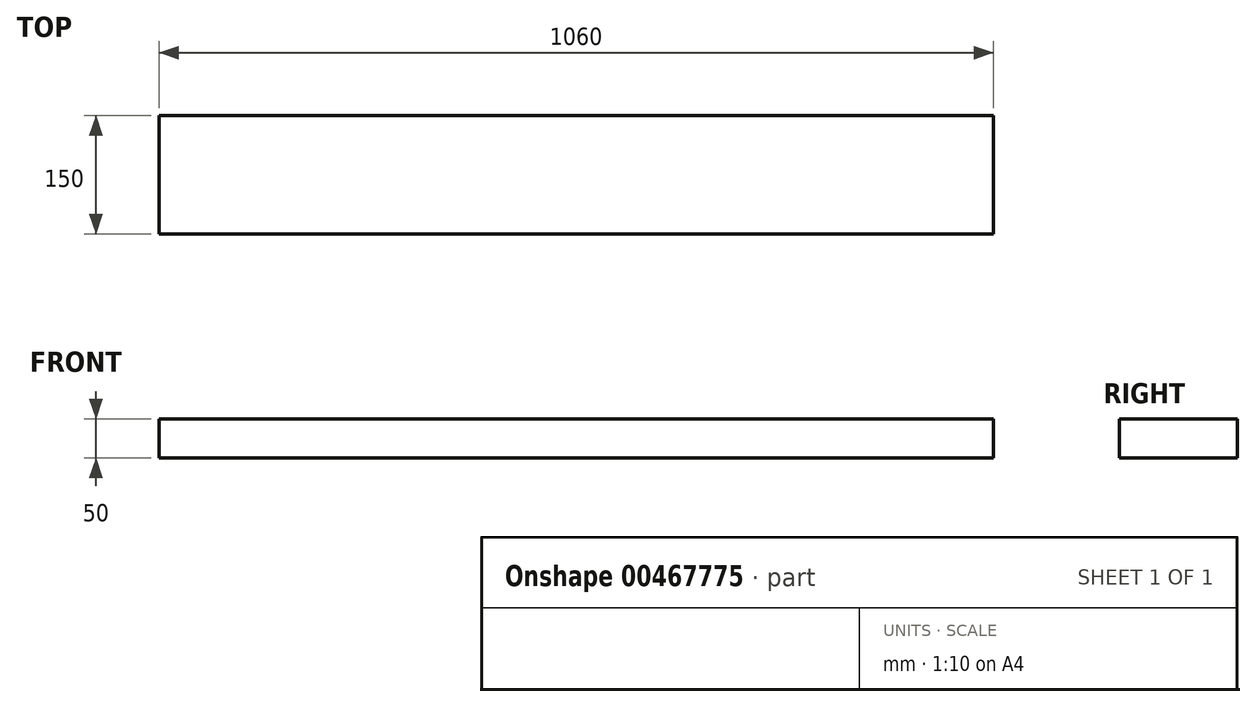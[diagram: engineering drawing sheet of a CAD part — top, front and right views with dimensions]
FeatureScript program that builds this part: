
annotation { "Feature Type Name" : "Feature", "Feature Type Description" : "" }
export const myFeature = defineFeature(function(context is Context, id is Id, definition is map)
    precondition{}
    {
        {
            var Q0;
            Q0=qCreatedBy(makeId("Top.planeOp"),FACE);
            var sketch = newSketch(context, id + "F0", { "sketchPlane" : qUnion([Q0])});
            skLineSegment(sketch, "E0.bottom", {"start": v(-509.87, -280.53) * mm, "end": v(550.13, -280.53) * mm});
            skLineSegment(sketch, "E0.top", {"start": v(-509.87, -130.53) * mm, "end": v(550.13, -130.53) * mm});
            skLineSegment(sketch, "E0.left", {"start": v(-509.87, -280.53) * mm, "end": v(-509.87, -130.53) * mm});
            skLineSegment(sketch, "E0.right", {"start": v(550.13, -280.53) * mm, "end": v(550.13, -130.53) * mm});
            skSolve(sketch);
        }
        {
            var Q0;
            Q0=qSketchRegion(id+"F0",true);
            extrude(context, id + "F1", {"entities" : qUnion([Q0]), "depth" : 50 * mm});
        }
    });
